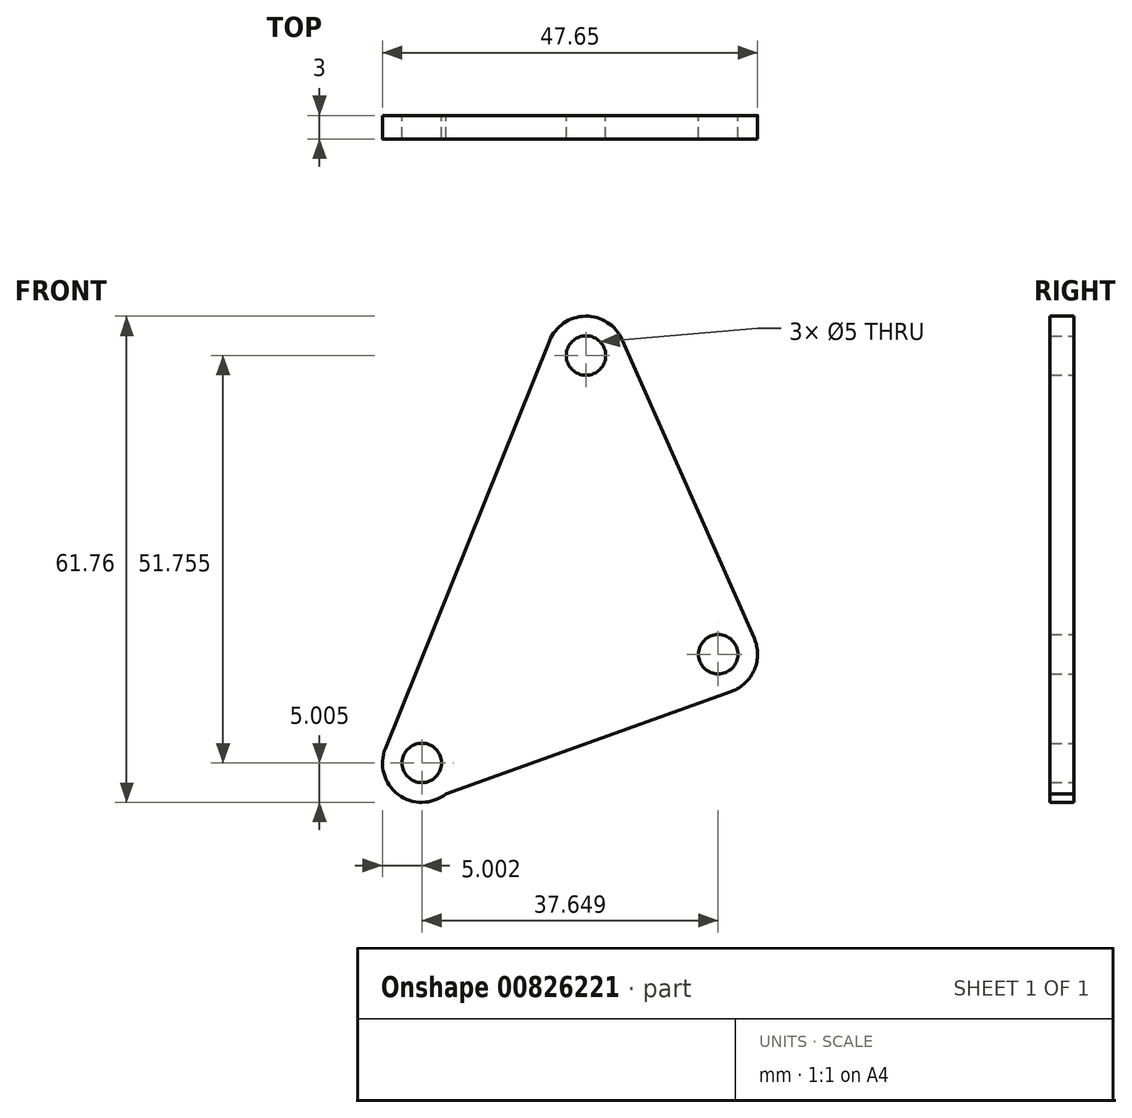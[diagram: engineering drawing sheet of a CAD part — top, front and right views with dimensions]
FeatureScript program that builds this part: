
annotation { "Feature Type Name" : "Feature", "Feature Type Description" : "" }
export const myFeature = defineFeature(function(context is Context, id is Id, definition is map)
    precondition{}
    {
        {
            var Q0;
            Q0=qCreatedBy(makeId("Front.planeOp"),FACE);
            var sketch = newSketch(context, id + "F0", { "sketchPlane" : qUnion([Q0])});
            skArc(sketch, "E0", {"start": v(4.57, 33.32) * mm, "mid": v(-0.08, 36.3) * mm, "end": v(-4.64, 33.17) * mm});
            skArc(sketch, "E1", {"start": v(18.48, -11.36) * mm, "mid": v(21.39, -8.62) * mm, "end": v(21.36, -4.63) * mm});
            skArc(sketch, "E2", {"start": v(-25.5, -18.59) * mm, "mid": v(-23.86, -24.45) * mm, "end": v(-17.78, -24.4) * mm});
            skLineSegment(sketch, "E3", {"start": v(-25.5, -18.59) * mm, "end": v(-4.64, 33.17) * mm});
            skLineSegment(sketch, "E4", {"start": v(-17.78, -24.4) * mm, "end": v(18.48, -11.36) * mm});
            skLineSegment(sketch, "E5", {"start": v(21.36, -4.63) * mm, "end": v(4.57, 33.32) * mm});
            skCircle(sketch, "E6", {"center": v(0, 31.3) * mm, "radius": 2.5 * mm});
            skCircle(sketch, "E7", {"center": v(16.8, -6.65) * mm, "radius": 2.5 * mm});
            skCircle(sketch, "E8", {"center": v(-20.86, -20.46) * mm, "radius": 2.5 * mm});
            skSolve(sketch);
        }
        {
            var Q0;
            Q0 = qSketchRegion(id + "F0", true);
            extrude(context, id + "F1", {"entities" : qUnion([Q0]), "depth" : 3 * mm, "offsetDistance" : 25 * mm});
        }
    });
